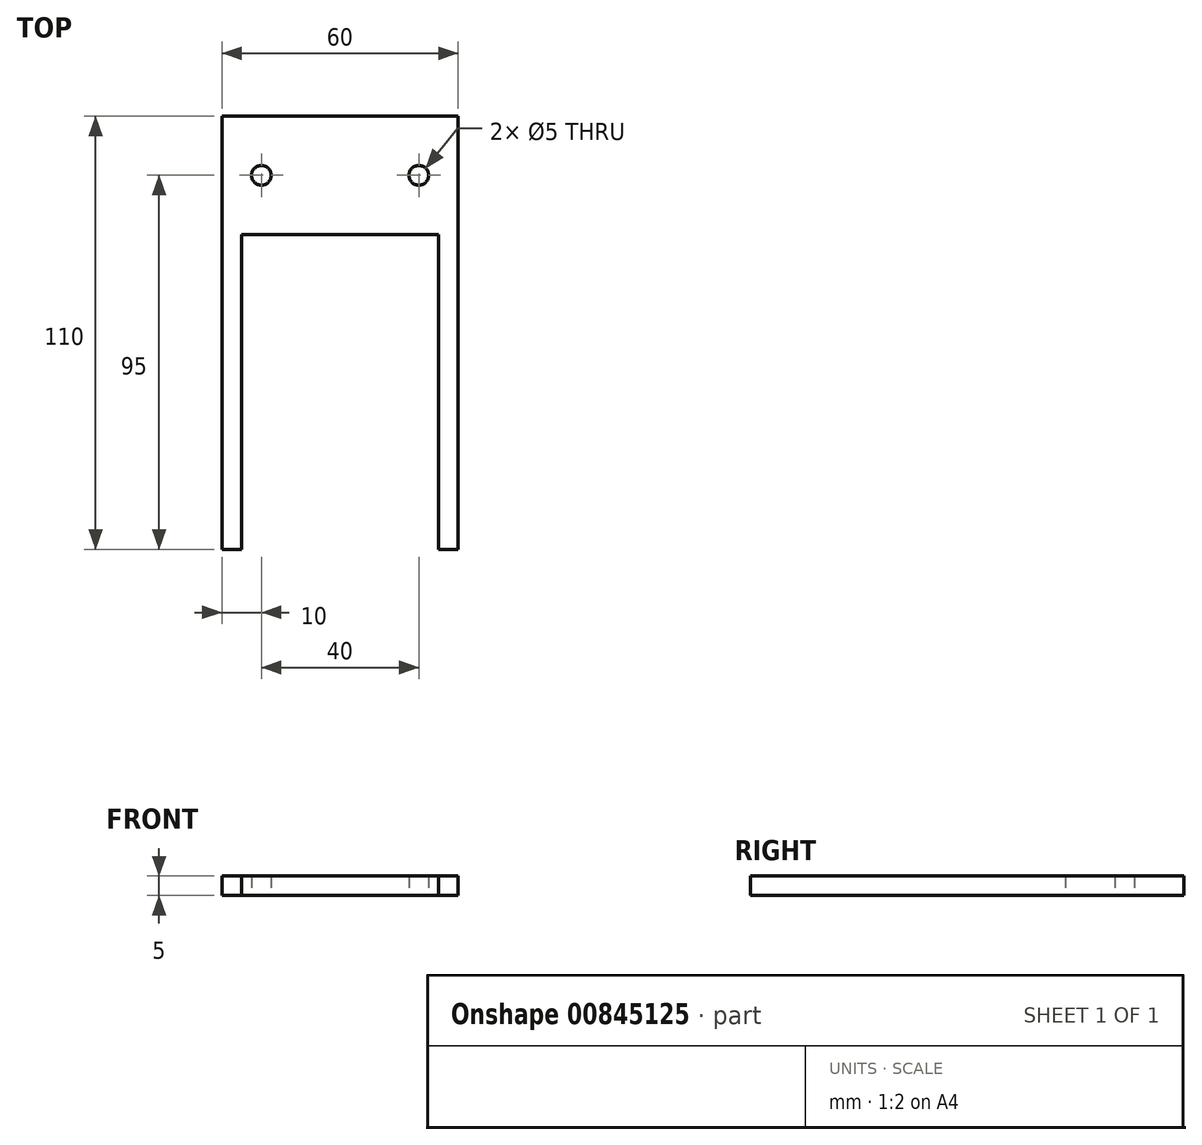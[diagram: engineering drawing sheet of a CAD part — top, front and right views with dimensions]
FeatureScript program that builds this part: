
annotation { "Feature Type Name" : "Feature", "Feature Type Description" : "" }
export const myFeature = defineFeature(function(context is Context, id is Id, definition is map)
    precondition{}
    {
        {
            var Q0;
            Q0=qCreatedBy(makeId("Top.planeOp"),FACE);
            var sketch = newSketch(context, id + "F0", { "sketchPlane" : qUnion([Q0])});
            skLineSegment(sketch, "E0.bottom", {"start": v(30, 15) * mm, "end": v(-30, 15) * mm});
            skLineSegment(sketch, "E0.top", {"start": v(30, -15) * mm, "end": v(-30, -15) * mm});
            skLineSegment(sketch, "E0.left", {"start": v(30, 15) * mm, "end": v(30, -15) * mm});
            skLineSegment(sketch, "E0.right", {"start": v(-30, 15) * mm, "end": v(-30, -15) * mm});
            skPoint(sketch, "E0.middle", {"position": v(0, 0) * mm});
            skLineSegment(sketch, "E1.bottom", {"start": v(-30, -15) * mm, "end": v(-25, -15) * mm});
            skLineSegment(sketch, "E1.top", {"start": v(-30, -95) * mm, "end": v(-25, -95) * mm});
            skLineSegment(sketch, "E1.left", {"start": v(-30, -15) * mm, "end": v(-30, -95) * mm});
            skLineSegment(sketch, "E1.right", {"start": v(-25, -15) * mm, "end": v(-25, -95) * mm});
            skLineSegment(sketch, "E2.bottom", {"start": v(30, -15) * mm, "end": v(25, -15) * mm});
            skLineSegment(sketch, "E2.top", {"start": v(30, -95) * mm, "end": v(25, -95) * mm});
            skLineSegment(sketch, "E2.left", {"start": v(30, -15) * mm, "end": v(30, -95) * mm});
            skLineSegment(sketch, "E2.right", {"start": v(25, -15) * mm, "end": v(25, -95) * mm});
            skLineSegment(sketch, "E3", {"start": v(-30, 0) * mm, "end": v(30, 0) * mm, "construction": true});
            skLineSegment(sketch, "E4", {"start": v(-20, 15) * mm, "end": v(-20, -15) * mm, "construction": true});
            skLineSegment(sketch, "E5", {"start": v(20, -15) * mm, "end": v(20, 15) * mm, "construction": true});
            skCircle(sketch, "E6", {"center": v(-20, 0) * mm, "radius": 2.5 * mm});
            skCircle(sketch, "E7", {"center": v(20, 0) * mm, "radius": 2.5 * mm});
            skSolve(sketch);
        }
        {
            var Q0;
            Q0 = qSketchRegion(id + "F0", true);
            extrude(context, id + "F1", {"entities" : qUnion([Q0]), "depth" : 5 * mm, "offsetDistance" : 25 * mm});
        }
    });
